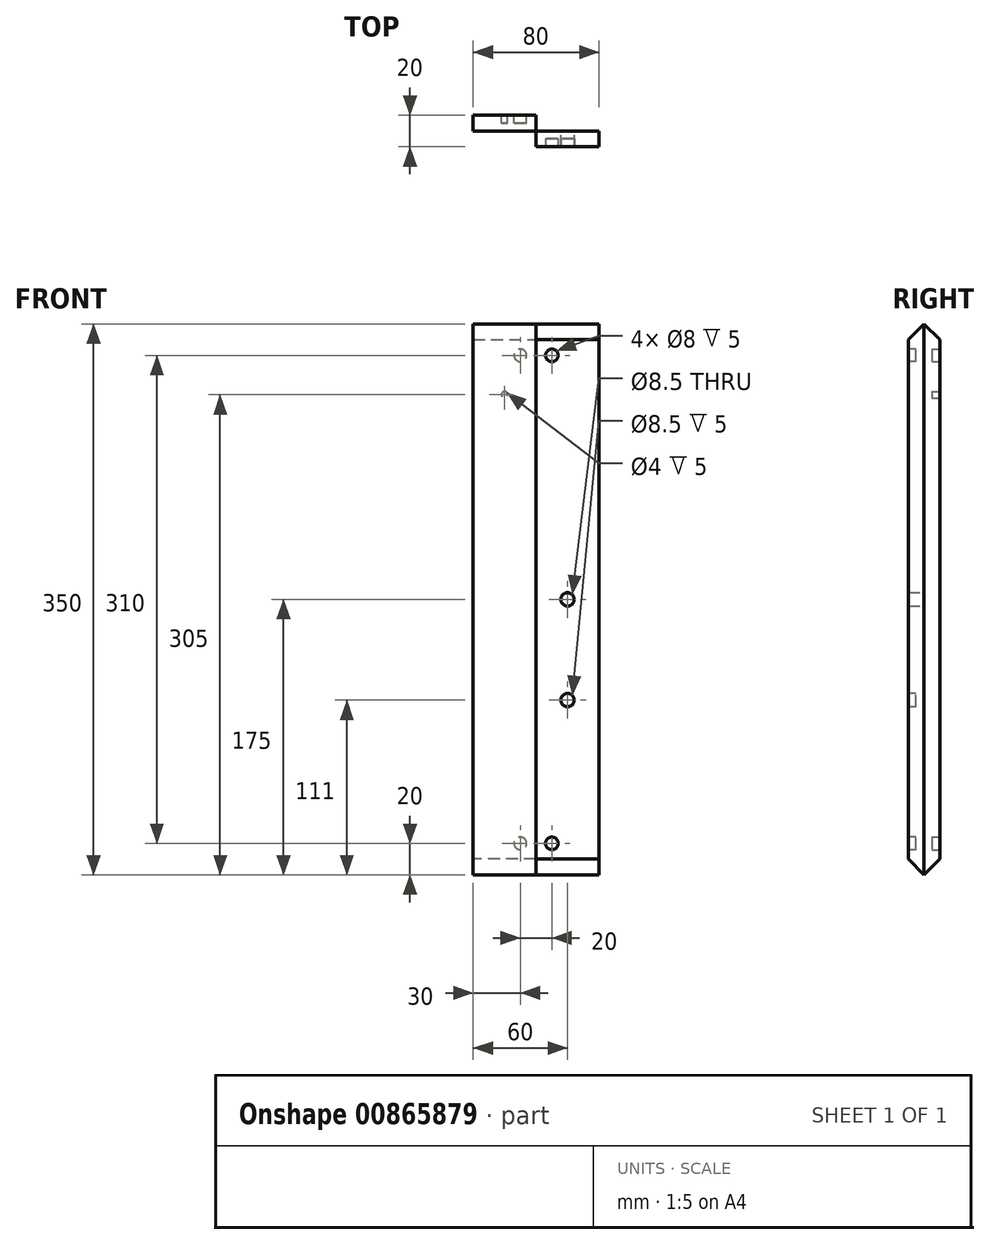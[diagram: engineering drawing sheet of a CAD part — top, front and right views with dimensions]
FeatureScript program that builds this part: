
annotation { "Feature Type Name" : "Feature", "Feature Type Description" : "" }
export const myFeature = defineFeature(function(context is Context, id is Id, definition is map)
    precondition{}
    {
        {
            var Q0;
            Q0=qCreatedBy(makeId("Top.planeOp"),FACE);
            var sketch = newSketch(context, id + "F0", { "sketchPlane" : qUnion([Q0])});
            skLineSegment(sketch, "E0.bottom", {"start": v(0, 0) * mm, "end": v(-40, 0) * mm});
            skLineSegment(sketch, "E0.top", {"start": v(0, 10) * mm, "end": v(-40, 10) * mm});
            skLineSegment(sketch, "E0.left", {"start": v(0, 0) * mm, "end": v(0, 10) * mm});
            skLineSegment(sketch, "E0.right", {"start": v(-40, 0) * mm, "end": v(-40, 10) * mm});
            skSolve(sketch);
        }
        {
            var Q0;
            Q0 = qSketchRegion(id + "F0", true);
            extrude(context, id + "F1", {"entities" : qUnion([Q0]), "depth" : 350 * mm, "offsetDistance" : 25 * mm});
        }
        {
            var Q0;
            Q0=makeQuery(id+"F1.opExtrude","CAP_EDGE",EDGE,{"disambiguationData":[OSD([sQuery(id+"F0.wireOp",EDGE,"E0.top")])],"isStart":false});
            chamfer(context, id + "F2", {"entities" : qUnion([Q0]), "width" : 10 * mm, "tangentPropagation" : true});
        }
        {
            var Q0;
            Q0=makeQuery(id+"F1.opExtrude","CAP_EDGE",EDGE,{"disambiguationData":[OSD([sQuery(id+"F0.wireOp",EDGE,"E0.top")])],"isStart":true});
            chamfer(context, id + "F3", {"entities" : qUnion([Q0]), "width" : 10 * mm, "tangentPropagation" : true});
        }
        {
            var Q0;
            Q0=qCreatedBy(makeId("Top.planeOp"),FACE);
            var sketch = newSketch(context, id + "F4", { "sketchPlane" : qUnion([Q0])});
            skLineSegment(sketch, "E1.bottom", {"start": v(0, 0) * mm, "end": v(40, 0) * mm});
            skLineSegment(sketch, "E1.top", {"start": v(0, -10) * mm, "end": v(40, -10) * mm});
            skLineSegment(sketch, "E1.left", {"start": v(0, 0) * mm, "end": v(0, -10) * mm});
            skLineSegment(sketch, "E1.right", {"start": v(40, 0) * mm, "end": v(40, -10) * mm});
            skSolve(sketch);
        }
        {
            var Q0;
            Q0 = qSketchRegion(id + "F4", true);
            extrude(context, id + "F5", {"entities" : qUnion([Q0]), "depth" : 350 * mm, "offsetDistance" : 25 * mm});
        }
        {
            var Q0;
            Q0=makeQuery(id+"F5.opExtrude","CAP_EDGE",EDGE,{"disambiguationData":[OSD([sQuery(id+"F4.wireOp",EDGE,"E1.top")])],"isStart":true});
            chamfer(context, id + "F6", {"entities" : qUnion([Q0]), "width" : 10 * mm, "tangentPropagation" : true});
        }
        {
            var Q0;
            Q0=makeQuery(id+"F5.opExtrude","CAP_EDGE",EDGE,{"disambiguationData":[OSD([sQuery(id+"F4.wireOp",EDGE,"E1.top")])],"isStart":false});
            chamfer(context, id + "F7", {"entities" : qUnion([Q0]), "width" : 10 * mm, "tangentPropagation" : true});
        }
        {
            var Q0;
            Q0=makeQuery(id+"F5.opExtrude","SWEPT_FACE",FACE,{"disambiguationData":[OSD([sQuery(id+"F4.wireOp",EDGE,"E1.bottom")])]});
            var sketch = newSketch(context, id + "F8", { "sketchPlane" : qUnion([Q0])});
            skCircle(sketch, "E2", {"center": v(-20, 175) * mm, "radius": 4.25 * mm});
            skSolve(sketch);
        }
        {
            var Q0;
            Q0 = qSketchRegion(id + "F8", true);
            extrude(context, id + "F9", {"entities" : qUnion([Q0]), "operationType" : NewBodyOperationType.REMOVE, "endBound" : BoundingType.THROUGH_ALL, "oppositeDirection" : true, "depth" : 25 * mm, "offsetDistance" : 25 * mm});
        }
        {
            var Q0;
            Q0=makeQuery(id+"F1.opExtrude","SWEPT_FACE",FACE,{"disambiguationData":[OSD([sQuery(id+"F0.wireOp",EDGE,"E0.top")])]});
            var sketch = newSketch(context, id + "F10", { "sketchPlane" : qUnion([Q0])});
            skCircle(sketch, "E3", {"center": v(20, 305) * mm, "radius": 2 * mm});
            skPoint(sketch, "E3.centerSnap0", {"position": v(20, 10) * mm});
            skCircle(sketch, "E4", {"center": v(10, 330) * mm, "radius": 4 * mm});
            skCircle(sketch, "E5", {"center": v(10, 20) * mm, "radius": 4 * mm});
            skSolve(sketch);
        }
        {
            var Q0;
            Q0 = qSketchRegion(id + "F10", true);
            extrude(context, id + "F11", {"entities" : qUnion([Q0]), "operationType" : NewBodyOperationType.REMOVE, "oppositeDirection" : true, "depth" : 5 * mm, "offsetDistance" : 25 * mm});
        }
        {
            var Q0;
            Q0=makeQuery(id+"F5.opExtrude","SWEPT_FACE",FACE,{"disambiguationData":[OSD([sQuery(id+"F4.wireOp",EDGE,"E1.top")])]});
            var sketch = newSketch(context, id + "F12", { "sketchPlane" : qUnion([Q0])});
            skCircle(sketch, "E6", {"center": v(20, 111) * mm, "radius": 4.25 * mm});
            skPoint(sketch, "E6.centerSnap0", {"position": v(20, 10) * mm});
            skCircle(sketch, "E7", {"center": v(10, 20) * mm, "radius": 4 * mm});
            skCircle(sketch, "E8", {"center": v(10, 330) * mm, "radius": 4 * mm});
            skSolve(sketch);
        }
        {
            var Q0;
            Q0 = qSketchRegion(id + "F12", true);
            extrude(context, id + "F13", {"entities" : qUnion([Q0]), "operationType" : NewBodyOperationType.REMOVE, "oppositeDirection" : true, "depth" : 5 * mm, "offsetDistance" : 25 * mm});
        }
    });
